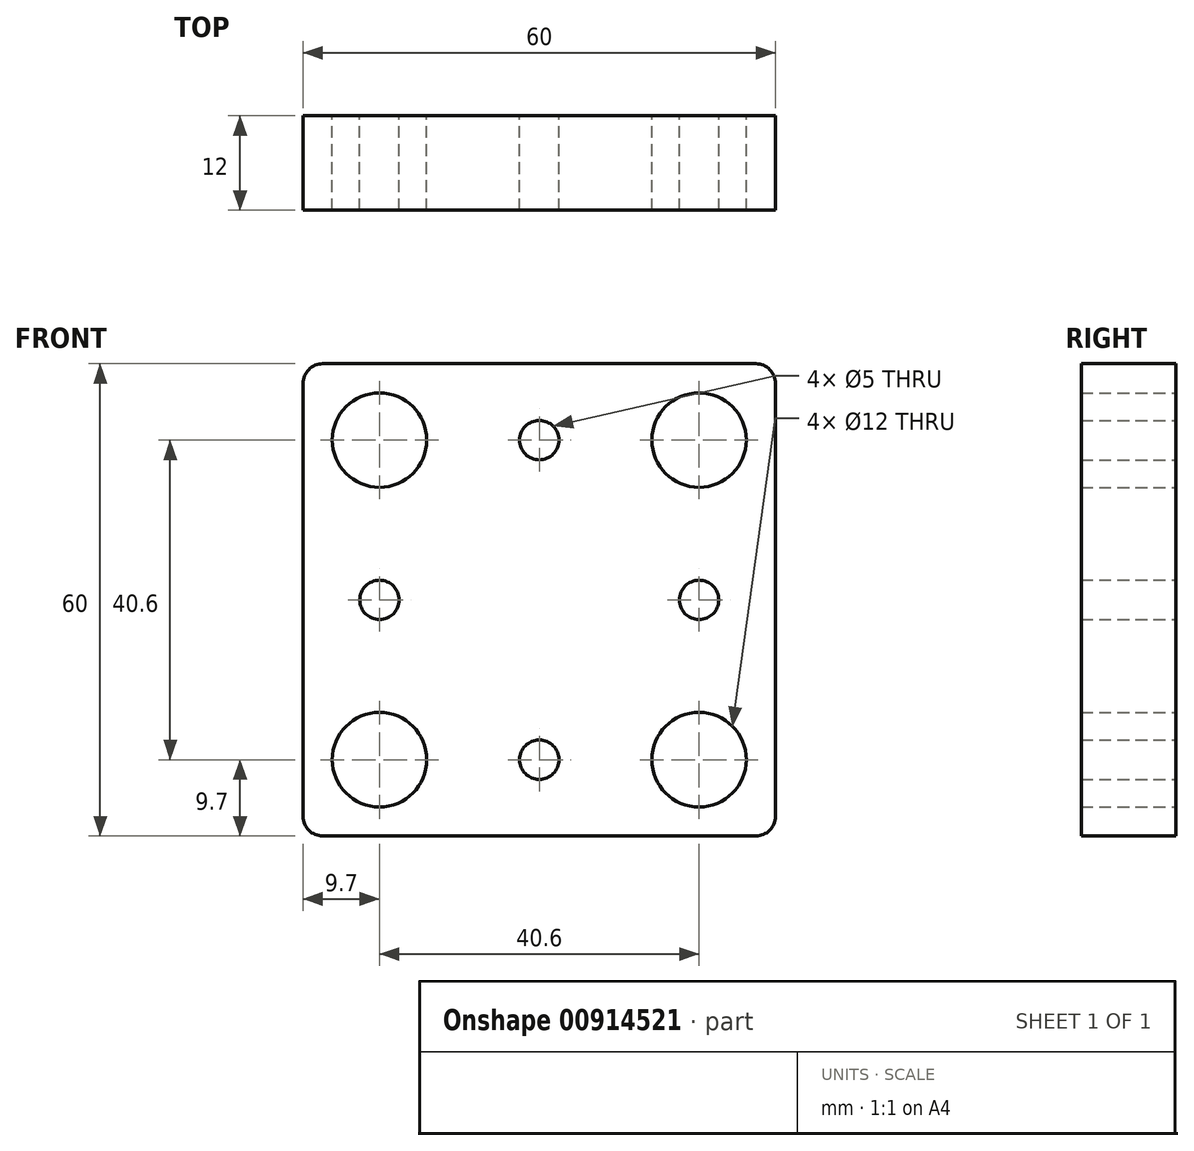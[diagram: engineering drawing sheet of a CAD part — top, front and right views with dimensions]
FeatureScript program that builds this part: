
annotation { "Feature Type Name" : "Feature", "Feature Type Description" : "" }
export const myFeature = defineFeature(function(context is Context, id is Id, definition is map)
    precondition{}
    {
        {
            var Q0;
            Q0=qCreatedBy(makeId("Front.planeOp"),FACE);
            var sketch = newSketch(context, id + "F0", { "sketchPlane" : qUnion([Q0])});
            skLineSegment(sketch, "E0.bottom", {"start": v(30, 30) * mm, "end": v(-30, 30) * mm});
            skLineSegment(sketch, "E0.top", {"start": v(30, -30) * mm, "end": v(-30, -30) * mm});
            skLineSegment(sketch, "E0.left", {"start": v(30, 30) * mm, "end": v(30, -30) * mm});
            skLineSegment(sketch, "E0.right", {"start": v(-30, 30) * mm, "end": v(-30, -30) * mm});
            skPoint(sketch, "E0.middle", {"position": v(0, 0) * mm});
            skLineSegment(sketch, "E1", {"start": v(20.3, 30) * mm, "end": v(20.3, -30) * mm, "construction": true});
            skLineSegment(sketch, "E2", {"start": v(30, 20.3) * mm, "end": v(-30, 20.3) * mm, "construction": true});
            skLineSegment(sketch, "E3.MirrorCS", {"start": v(-20.3, 30) * mm, "end": v(-20.3, -30) * mm, "construction": true});
            skLineSegment(sketch, "E4.MirrorCS", {"start": v(30, -20.3) * mm, "end": v(-30, -20.3) * mm, "construction": true});
            skPoint(sketch, "E5", {"position": v(-20.3, 20.3) * mm});
            skPoint(sketch, "E6", {"position": v(20.3, 20.3) * mm});
            skPoint(sketch, "E7", {"position": v(20.3, -20.3) * mm});
            skPoint(sketch, "E8", {"position": v(-20.3, -20.3) * mm});
            skPoint(sketch, "E9", {"position": v(0, 20.3) * mm});
            skPoint(sketch, "E10", {"position": v(0, -20.3) * mm});
            skPoint(sketch, "E11", {"position": v(-20.3, 0) * mm});
            skPoint(sketch, "E12", {"position": v(20.3, 0) * mm});
            skSolve(sketch);
        }
        {
            var Q0;
            Q0=qSketchRegion(id+"F0",true);
            extrude(context, id + "F1", {"entities" : qUnion([Q0]), "depth" : 12 * mm, "offsetDistance" : 25 * mm});
        }
        {
            var Q0;
            Q0=sQuery(id+"F0.wireOp",VERTEX,"E9");
            var Q1;
            Q1=sQuery(id+"F0.wireOp",VERTEX,"E10");
            var Q2;
            Q2=sQuery(id+"F0.wireOp",VERTEX,"E11");
            var Q3;
            Q3=sQuery(id+"F0.wireOp",VERTEX,"E12");
            var Q4;
            Q4=makeQuery(id+"F1.opExtrude","SWEPT_BODY",BODY,{"disambiguationData":[OSD([sQuery(id+"F0.wireOp",EDGE,"E0.bottom"),sQuery(id+"F0.wireOp",EDGE,"E0.top"),sQuery(id+"F0.wireOp",EDGE,"E0.left"),sQuery(id+"F0.wireOp",EDGE,"E0.right")])]});
            hole(context, id + "F2", {"style" : HoleStyle.SIMPLE, "endStyle" : HoleEndStyle.THROUGH, "oppositeDirection" : true, "holeDiameter" : 5 * mm, "majorDiameter" : 5 * mm, "isTappedThrough" : true, "tappedDepth" : 12 * mm, "tapClearance" : 3, "locations" : qUnion([Q0, Q1, Q2, Q3]), "scope" : qUnion([Q4])});
        }
        {
            var Q0;
            Q0=sQuery(id+"F0.wireOp",VERTEX,"E5");
            var Q1;
            Q1=sQuery(id+"F0.wireOp",VERTEX,"E6");
            var Q2;
            Q2=sQuery(id+"F0.wireOp",VERTEX,"E7");
            var Q3;
            Q3=sQuery(id+"F0.wireOp",VERTEX,"E8");
            var Q4;
            Q4=makeQuery(id+"F1.opExtrude","SWEPT_BODY",BODY,{"disambiguationData":[OSD([sQuery(id+"F0.wireOp",EDGE,"E0.bottom"),sQuery(id+"F0.wireOp",EDGE,"E0.top"),sQuery(id+"F0.wireOp",EDGE,"E0.left"),sQuery(id+"F0.wireOp",EDGE,"E0.right")])]});
            hole(context, id + "F3", {"style" : HoleStyle.SIMPLE, "endStyle" : HoleEndStyle.THROUGH, "oppositeDirection" : true, "holeDiameter" : 12 * mm, "majorDiameter" : 5 * mm, "isTappedThrough" : true, "tappedDepth" : 12 * mm, "tapClearance" : 3, "locations" : qUnion([Q0, Q1, Q2, Q3]), "scope" : qUnion([Q4])});
        }
        {
            var Q0;
            Q0=makeQuery(id+"F1.opExtrude","SWEPT_EDGE",EDGE,{"disambiguationData":[OSD([sQuery(id+"F0.wireOp",EDGE,"E0.bottom"),sQuery(id+"F0.wireOp",EDGE,"E0.left")])]});
            var Q1;
            Q1=makeQuery(id+"F1.opExtrude","SWEPT_EDGE",EDGE,{"disambiguationData":[OSD([sQuery(id+"F0.wireOp",EDGE,"E0.top"),sQuery(id+"F0.wireOp",EDGE,"E0.left")])]});
            var Q2;
            Q2=makeQuery(id+"F1.opExtrude","SWEPT_EDGE",EDGE,{"disambiguationData":[OSD([sQuery(id+"F0.wireOp",EDGE,"E0.top"),sQuery(id+"F0.wireOp",EDGE,"E0.right")])]});
            var Q3;
            Q3=makeQuery(id+"F1.opExtrude","SWEPT_EDGE",EDGE,{"disambiguationData":[OSD([sQuery(id+"F0.wireOp",EDGE,"E0.bottom"),sQuery(id+"F0.wireOp",EDGE,"E0.right")])]});
            fillet(context, id + "F4", {"entities" : qUnion([Q0, Q1, Q2, Q3]), "radius" : 2.5 * mm, "tangentPropagation" : true, "allowEdgeOverflow" : false});
        }
    });
